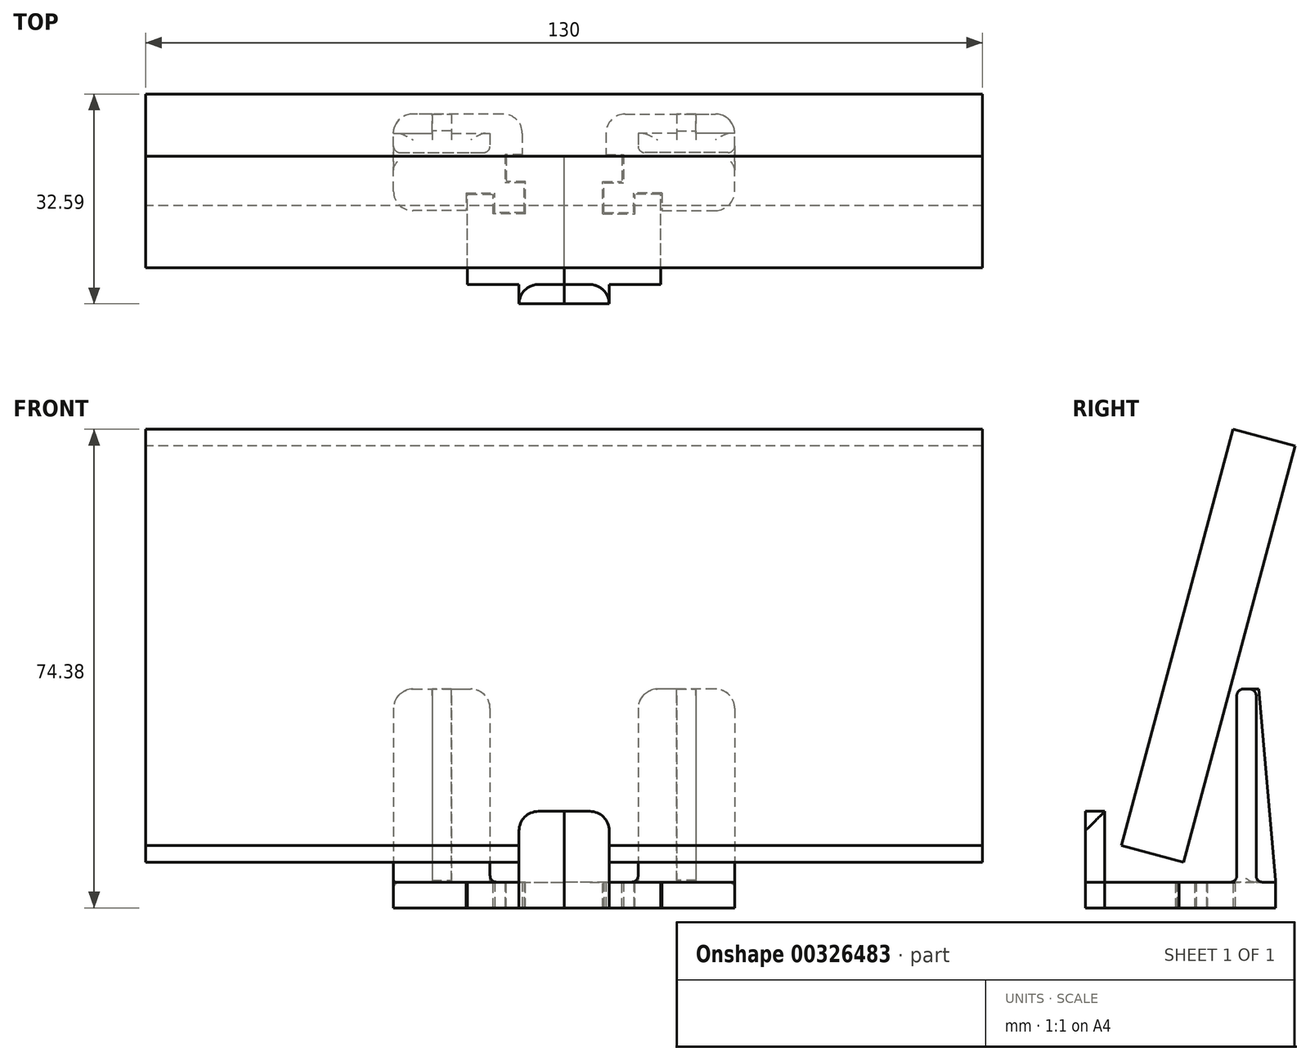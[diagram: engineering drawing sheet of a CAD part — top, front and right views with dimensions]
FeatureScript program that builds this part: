
annotation { "Feature Type Name" : "Feature", "Feature Type Description" : "" }
export const myFeature = defineFeature(function(context is Context, id is Id, definition is map)
    precondition{}
    {
        {
            var Q0;
            Q0=qCreatedBy(makeId("Front.planeOp"),FACE);
            var sketch = newSketch(context, id + "F0", { "sketchPlane" : qUnion([Q0])});
            skLineSegment(sketch, "E0", {"start": v(-35.67, 0) * mm, "end": v(38.03, 0) * mm, "construction": true});
            skSolve(sketch);
        }
        {
            var Q0;
            Q0=sQuery(id+"F0.wireOp",EDGE,"E0");
            cPlane(context, id + "F1", {"entities" : qUnion([Q0]), "cplaneType" : CPlaneType.LINE_ANGLE, "offset" : 25 * mm, "angle" : 345 * degree, "width" : 150 * mm, "height" : 150 * mm});
        }
        {
            var Q0;
            Q0=qCreatedBy(id+"F1.planeOp",FACE);
            var sketch = newSketch(context, id + "F2", { "sketchPlane" : qUnion([Q0])});
            skLineSegment(sketch, "E1.bottom", {"start": v(-65, 77) * mm, "end": v(65, 77) * mm});
            skLineSegment(sketch, "E1.top", {"start": v(-65, 10) * mm, "end": v(65, 10) * mm});
            skLineSegment(sketch, "E1.left", {"start": v(-65, 77) * mm, "end": v(-65, 10) * mm});
            skLineSegment(sketch, "E1.right", {"start": v(65, 77) * mm, "end": v(65, 10) * mm});
            skPoint(sketch, "E2", {"position": v(0, 10) * mm});
            skSolve(sketch);
        }
        {
            var Q0;
            Q0 = qSketchRegion(id + "F2", true);
            extrude(context, id + "F3", {"entities" : qUnion([Q0]), "depth" : 10 * mm});
        }
        {
            var Q0;
            Q0=qCreatedBy(makeId("Right.planeOp"),FACE);
            var sketch = newSketch(context, id + "F4", { "sketchPlane" : qUnion([Q0])});
            skLineSegment(sketch, "E3.bottom", {"start": v(0, 0) * mm, "end": v(20, 0) * mm});
            skLineSegment(sketch, "E3.top", {"start": v(0, 4) * mm, "end": v(20, 4) * mm});
            skLineSegment(sketch, "E3.left", {"start": v(0, 0) * mm, "end": v(0, 4) * mm});
            skLineSegment(sketch, "E3.right", {"start": v(20, 0) * mm, "end": v(20, 4) * mm});
            skLineSegment(sketch, "E4.bottom", {"start": v(0, 0) * mm, "end": v(-3, 0) * mm});
            skLineSegment(sketch, "E4.top", {"start": v(0, 15) * mm, "end": v(-3, 15) * mm});
            skLineSegment(sketch, "E4.left", {"start": v(0, 0) * mm, "end": v(0, 15) * mm});
            skLineSegment(sketch, "E4.right", {"start": v(-3, 0) * mm, "end": v(-3, 15) * mm});
            skSolve(sketch);
        }
        {
            var Q0;
            {var subQ0=sQuery(id+"F4.wireOp",EDGE,"E3.bottom");Q0=makeQuery(id+"F4.imprint","IMPRINT",FACE,{"disambiguationData":[TD([[makeQuery(id+"F4.imprint","IMPRINT",EDGE,{"derivedFrom":subQ0}),1.0]])]});}
            extrude(context, id + "F5", {"entities" : qUnion([Q0]), "oppositeDirection" : true, "depth" : 15 * mm});
        }
        {
            var Q0;
            {var subQ3=sQuery(id+"F4.wireOp",EDGE,"E4.bottom");Q0=makeQuery(id+"F4.imprint","IMPRINT",FACE,{"disambiguationData":[TD([[makeQuery(id+"F4.imprint","IMPRINT",EDGE,{"derivedFrom":subQ3}),-1.0]])]});}
            extrude(context, id + "F6", {"entities" : qUnion([Q0]), "operationType" : NewBodyOperationType.ADD, "oppositeDirection" : true, "depth" : 7 * mm});
        }
        {
            var Q0;
            {var subQ0=makeQuery(id+"F5.opExtrude","SWEPT_FACE",FACE,{"disambiguationData":[OSD([sQuery(id+"F4.wireOp",EDGE,"E3.top")])]});Q0=makeQuery(id+"F9.boolean.opBoolean","MERGE",FACE,{"derivedFrom":[subQ0,makeQuery(id+"F9.opPattern","COPY",FACE,{"derivedFrom":subQ0,"instanceName":"1"})]});}
            var sketch = newSketch(context, id + "F7", { "sketchPlane" : qUnion([Q0])});
            skLineSegment(sketch, "E5.bottom", {"start": v(-15, 20) * mm, "end": v(-9, 20) * mm});
            skLineSegment(sketch, "E5.top", {"start": v(-15, 14) * mm, "end": v(-9, 14) * mm});
            skLineSegment(sketch, "E5.left", {"start": v(-15, 20) * mm, "end": v(-15, 14) * mm});
            skLineSegment(sketch, "E5.right", {"start": v(-9, 20) * mm, "end": v(-9, 14) * mm});
            skLineSegment(sketch, "E6.bottom", {"start": v(-6, 11) * mm, "end": v(-11, 11) * mm});
            skLineSegment(sketch, "E6.top", {"start": v(-6, 16) * mm, "end": v(-11, 16) * mm});
            skLineSegment(sketch, "E6.left", {"start": v(-6, 11) * mm, "end": v(-6, 16) * mm});
            skLineSegment(sketch, "E6.right", {"start": v(-11, 11) * mm, "end": v(-11, 16) * mm});
            skSolve(sketch);
        }
        {
            var Q0;
            Q0 = qSketchRegion(id + "F7", true);
            extrude(context, id + "F8", {"entities" : qUnion([Q0]), "operationType" : NewBodyOperationType.REMOVE, "endBound" : BoundingType.UP_TO_NEXT, "oppositeDirection" : true, "depth" : 25 * mm});
        }
        {
            var Q0;
            Q0=makeQuery(id+"F5.opExtrude","SWEPT_BODY",BODY,{"disambiguationData":[OSD([sQuery(id+"F4.wireOp",EDGE,"E3.bottom"),sQuery(id+"F4.wireOp",EDGE,"E3.top"),sQuery(id+"F4.wireOp",EDGE,"E3.right"),sQuery(id+"F4.wireOp",EDGE,"E4.left")])]});
            var Q1;
            {var subQ0=sQuery(id+"F4.wireOp",EDGE,"E3.bottom");Q1=makeQuery(id+"F4.imprint","IMPRINT",FACE,{"disambiguationData":[TD([[makeQuery(id+"F4.imprint","IMPRINT",EDGE,{"derivedFrom":subQ0}),1.0]])]});}
            mirror(context, id + "F9", {"operationType" : NewBodyOperationType.ADD, "entities" : qUnion([Q0]), "mirrorPlane" : qUnion([Q1])});
        }
        {
            var Q0;
            Q0=qCreatedBy(makeId("Top.planeOp"),FACE);
            var sketch = newSketch(context, id + "F10", { "sketchPlane" : qUnion([Q0])});
            skLineSegment(sketch, "E7.top", {"start": v(-6.5, 26.5) * mm, "end": v(-26.5, 26.5) * mm});
            skLineSegment(sketch, "E7.right", {"start": v(-26.5, 11.5) * mm, "end": v(-26.5, 26.5) * mm});
            skLineSegment(sketch, "E8", {"start": v(-15.2, 11.5) * mm, "end": v(-26.5, 11.5) * mm});
            skLineSegment(sketch, "E9", {"start": v(-6.5, 26.5) * mm, "end": v(-6.5, 20.2) * mm});
            skLineSegment(sketch, "E10", {"start": v(-15, 14) * mm, "end": v(-15, 12.25) * mm, "construction": true});
            skLineSegment(sketch, "E11", {"start": v(-6.5, 20) * mm, "end": v(-9, 20) * mm, "construction": true});
            skLineSegment(sketch, "E12.0", {"start": v(-9, 20) * mm, "end": v(-9, 16) * mm, "construction": true});
            skLineSegment(sketch, "E13.0", {"start": v(-6, 16) * mm, "end": v(-9, 16) * mm, "construction": true});
            skLineSegment(sketch, "E14.0", {"start": v(-6, 11) * mm, "end": v(-6, 16) * mm, "construction": true});
            skLineSegment(sketch, "E15.0", {"start": v(-6, 11) * mm, "end": v(-11, 11) * mm, "construction": true});
            skLineSegment(sketch, "E16.0", {"start": v(-11, 11) * mm, "end": v(-11, 14) * mm, "construction": true});
            skLineSegment(sketch, "E17.0", {"start": v(-15, 14) * mm, "end": v(-11, 14) * mm, "construction": true});
            skLineSegment(sketch, "E18.0", {"start": v(-15.2, 14.2) * mm, "end": v(-15.2, 11.5) * mm});
            skLineSegment(sketch, "E18.1", {"start": v(-15.2, 14.2) * mm, "end": v(-10.8, 14.2) * mm});
            skLineSegment(sketch, "E18.2", {"start": v(-10.8, 11.2) * mm, "end": v(-10.8, 14.2) * mm});
            skLineSegment(sketch, "E18.3", {"start": v(-6.2, 11.2) * mm, "end": v(-10.8, 11.2) * mm});
            skLineSegment(sketch, "E18.4", {"start": v(-6.5, 20.2) * mm, "end": v(-9.2, 20.2) * mm});
            skLineSegment(sketch, "E18.5", {"start": v(-9.2, 20.2) * mm, "end": v(-9.2, 15.8) * mm});
            skLineSegment(sketch, "E18.6", {"start": v(-6.2, 15.8) * mm, "end": v(-9.2, 15.8) * mm});
            skLineSegment(sketch, "E18.7", {"start": v(-6.2, 11.2) * mm, "end": v(-6.2, 15.8) * mm});
            skSolve(sketch);
        }
        {
            var Q0;
            Q0 = qSketchRegion(id + "F10", true);
            extrude(context, id + "F11", {"entities" : qUnion([Q0]), "depth" : 4 * mm});
        }
        {
            var Q0;
            Q0=makeQuery(id+"F11.opExtrude","CAP_FACE",FACE,{"disambiguationData":[OSD([sQuery(id+"F10.wireOp",EDGE,"E7.top"),sQuery(id+"F10.wireOp",EDGE,"E7.right"),sQuery(id+"F10.wireOp",EDGE,"E8"),sQuery(id+"F10.wireOp",EDGE,"E9"),sQuery(id+"F10.wireOp",EDGE,"E18.0"),sQuery(id+"F10.wireOp",EDGE,"E18.1"),sQuery(id+"F10.wireOp",EDGE,"E18.2"),sQuery(id+"F10.wireOp",EDGE,"E18.3"),sQuery(id+"F10.wireOp",EDGE,"E18.4"),sQuery(id+"F10.wireOp",EDGE,"E18.5"),sQuery(id+"F10.wireOp",EDGE,"E18.6"),sQuery(id+"F10.wireOp",EDGE,"E18.7")])],"isStart":false});
            var sketch = newSketch(context, id + "F12", { "sketchPlane" : qUnion([Q0])});
            skLineSegment(sketch, "E19.bottom", {"start": v(-26.5, 23.5) * mm, "end": v(-11.5, 23.5) * mm});
            skLineSegment(sketch, "E19.top", {"start": v(-26.5, 20.5) * mm, "end": v(-11.5, 20.5) * mm});
            skLineSegment(sketch, "E19.left", {"start": v(-26.5, 23.5) * mm, "end": v(-26.5, 20.5) * mm});
            skLineSegment(sketch, "E19.right", {"start": v(-11.5, 23.5) * mm, "end": v(-11.5, 20.5) * mm});
            skPoint(sketch, "E20", {"position": v(-19, 23.5) * mm});
            skLineSegment(sketch, "E21.bottom", {"start": v(-17.5, 26.5) * mm, "end": v(-20.5, 26.5) * mm});
            skLineSegment(sketch, "E21.top", {"start": v(-17.5, 23.5) * mm, "end": v(-20.5, 23.5) * mm});
            skLineSegment(sketch, "E21.left", {"start": v(-17.5, 26.5) * mm, "end": v(-17.5, 23.5) * mm});
            skLineSegment(sketch, "E21.right", {"start": v(-20.5, 26.5) * mm, "end": v(-20.5, 23.5) * mm});
            skSolve(sketch);
        }
        {
            var Q0;
            Q0 = qSketchRegion(id + "F12", true);
            extrude(context, id + "F13", {"entities" : qUnion([Q0]), "operationType" : NewBodyOperationType.ADD, "depth" : 30 * mm});
        }
        {
            var Q0;
            Q0=makeQuery(id+"F13.opExtrude","CAP_EDGE",EDGE,{"disambiguationData":[OSD([sQuery(id+"F12.wireOp",EDGE,"E21.bottom")])],"isStart":false});
            chamfer(context, id + "F14", {"entities" : qUnion([Q0]), "chamferType" : ChamferType.OFFSET_ANGLE, "width" : 2.6 * mm, "oppositeDirection" : false, "angle" : 85 * degree, "tangentPropagation" : true});
        }
        {
            var Q0;
            Q0=makeQuery(id+"F11.opExtrude","SWEPT_EDGE",EDGE,{"disambiguationData":[OSD([sQuery(id+"F10.wireOp",EDGE,"E7.right"),sQuery(id+"F10.wireOp",EDGE,"E8")])]});
            var Q1;
            Q1=makeQuery(id+"F11.opExtrude","SWEPT_EDGE",EDGE,{"disambiguationData":[OSD([sQuery(id+"F10.wireOp",EDGE,"E7.top"),sQuery(id+"F10.wireOp",EDGE,"E7.right")])]});
            var Q2;
            Q2=makeQuery(id+"F5.opExtrude","CAP_EDGE",EDGE,{"disambiguationData":[OSD([sQuery(id+"F4.wireOp",EDGE,"E4.left")])],"isStart":false});
            var Q3;
            {var subQ0=sQuery(id+"F4.wireOp",EDGE,"E4.left");Q3=makeQuery(id+"F6.boolean.opBoolean","SPLIT",EDGE,{"disambiguationData":[topologyDisambiguationEdgeConnected([makeQuery(id+"F5.opExtrude","SWEPT_FACE",FACE,{"disambiguationData":[OSD([subQ0])]})])],"derivedFrom":makeQuery(id+"F6.opExtrude","CAP_EDGE",EDGE,{"disambiguationData":[OSD([subQ0])],"isStart":false})});}
            var Q4;
            {var subQ0=sQuery(id+"F4.wireOp",EDGE,"E4.left");Q4=makeQuery(id+"F9.opPattern","COPY",EDGE,{"derivedFrom":makeQuery(id+"F6.boolean.opBoolean","SPLIT",EDGE,{"disambiguationData":[topologyDisambiguationEdgeConnected([makeQuery(id+"F5.opExtrude","SWEPT_FACE",FACE,{"disambiguationData":[OSD([subQ0])]})])],"derivedFrom":makeQuery(id+"F6.opExtrude","CAP_EDGE",EDGE,{"disambiguationData":[OSD([subQ0])],"isStart":false})}),"instanceName":"1"});}
            var Q5;
            Q5=makeQuery(id+"F9.opPattern","COPY",EDGE,{"derivedFrom":makeQuery(id+"F5.opExtrude","CAP_EDGE",EDGE,{"disambiguationData":[OSD([sQuery(id+"F4.wireOp",EDGE,"E4.left")])],"isStart":false}),"instanceName":"1"});
            var Q6;
            Q6=makeQuery(id+"F11.opExtrude","SWEPT_EDGE",EDGE,{"disambiguationData":[OSD([sQuery(id+"F10.wireOp",EDGE,"E7.top"),sQuery(id+"F10.wireOp",EDGE,"E9")])]});
            var Q7;
            Q7=makeQuery(id+"F6.opExtrude","CAP_EDGE",EDGE,{"disambiguationData":[OSD([sQuery(id+"F4.wireOp",EDGE,"E4.top")])],"isStart":false});
            var Q8;
            Q8=makeQuery(id+"F9.opPattern","COPY",EDGE,{"derivedFrom":makeQuery(id+"F6.opExtrude","CAP_EDGE",EDGE,{"disambiguationData":[OSD([sQuery(id+"F4.wireOp",EDGE,"E4.top")])],"isStart":false}),"instanceName":"1"});
            var Q9;
            Q9=makeQuery(id+"F13.opExtrude","CAP_EDGE",EDGE,{"disambiguationData":[OSD([sQuery(id+"F12.wireOp",EDGE,"E19.left")])],"isStart":false});
            var Q10;
            Q10=makeQuery(id+"F13.opExtrude","CAP_EDGE",EDGE,{"disambiguationData":[OSD([sQuery(id+"F12.wireOp",EDGE,"E19.right")])],"isStart":false});
            fillet(context, id + "F15", {"entities" : qUnion([Q0, Q1, Q2, Q3, Q4, Q5, Q6, Q7, Q8, Q9, Q10]), "radius" : 3 * mm, "tangentPropagation" : true, "allowEdgeOverflow" : false});
        }
        {
            var Q0;
            Q0=makeQuery(id+"F13.opExtrude","SWEPT_FACE",FACE,{"disambiguationData":[OSD([sQuery(id+"F12.wireOp",EDGE,"E19.top")])]});
            var Q1;
            {var subQ0=makeQuery(id+"F6.opExtrude","SWEPT_FACE",FACE,{"disambiguationData":[OSD([sQuery(id+"F4.wireOp",EDGE,"E4.left")])]});Q1=makeQuery(id+"F9.boolean.opBoolean","MERGE",FACE,{"derivedFrom":[subQ0,makeQuery(id+"F9.opPattern","COPY",FACE,{"derivedFrom":subQ0,"instanceName":"1"})]});}
            var Q2;
            {var subQ0=makeQuery(id+"F6.opExtrude","SWEPT_EDGE",EDGE,{"disambiguationData":[OSD([sQuery(id+"F4.wireOp",EDGE,"E4.top"),sQuery(id+"F4.wireOp",EDGE,"E4.right")])]});Q2=makeQuery(id+"F9.boolean.opBoolean","MERGE",EDGE,{"derivedFrom":[subQ0,makeQuery(id+"F9.opPattern","COPY",EDGE,{"derivedFrom":subQ0,"instanceName":"1"})]});}
            var Q3;
            {var subQ0=sQuery(id+"F12.wireOp",EDGE,"E19.bottom");Q3=makeQuery(id+"F13.opExtrude","CAP_EDGE",EDGE,{"disambiguationData":[OSD([subQ0]),TDD([makeQuery(id+"F12.imprint","IMPRINT",EDGE,{"disambiguationData":[TD([[makeQuery(id+"F12.imprint","INTERSECT",VERTEX,{"derivedFrom":[subQ0,sQuery(id+"F12.wireOp",EDGE,"E19.right")]}),1.0]])],"derivedFrom":subQ0})])],"isStart":false});}
            var Q4;
            {var subQ0=sQuery(id+"F12.wireOp",EDGE,"E19.bottom");Q4=makeQuery(id+"F13.opExtrude","CAP_EDGE",EDGE,{"disambiguationData":[OSD([subQ0]),TDD([makeQuery(id+"F12.imprint","IMPRINT",EDGE,{"disambiguationData":[TD([[makeQuery(id+"F12.imprint","INTERSECT",VERTEX,{"derivedFrom":[makeQuery(id+"F11.opExtrude","CAP_EDGE",EDGE,{"disambiguationData":[OSD([sQuery(id+"F10.wireOp",EDGE,"E7.right")])],"isStart":false}),subQ0,sQuery(id+"F12.wireOp",EDGE,"E19.left")]}),-1.0]])],"derivedFrom":subQ0})])],"isStart":false});}
            var Q5;
            {var subQ0=sQuery(id+"F12.wireOp",EDGE,"E19.bottom");Q5=makeQuery(id+"F13.opExtrude","CAP_EDGE",EDGE,{"disambiguationData":[OSD([subQ0]),TDD([makeQuery(id+"F12.imprint","IMPRINT",EDGE,{"disambiguationData":[TD([[makeQuery(id+"F12.imprint","INTERSECT",VERTEX,{"derivedFrom":[makeQuery(id+"F11.opExtrude","CAP_EDGE",EDGE,{"disambiguationData":[OSD([sQuery(id+"F10.wireOp",EDGE,"E7.right")])],"isStart":false}),subQ0,sQuery(id+"F12.wireOp",EDGE,"E19.left")]}),-1.0]])],"derivedFrom":subQ0})])],"isStart":true});}
            var Q6;
            {var subQ0=sQuery(id+"F12.wireOp",EDGE,"E19.bottom");Q6=makeQuery(id+"F13.opExtrude","CAP_EDGE",EDGE,{"disambiguationData":[OSD([subQ0]),TDD([makeQuery(id+"F12.imprint","IMPRINT",EDGE,{"disambiguationData":[TD([[makeQuery(id+"F12.imprint","INTERSECT",VERTEX,{"derivedFrom":[subQ0,sQuery(id+"F12.wireOp",EDGE,"E19.right")]}),1.0]])],"derivedFrom":subQ0})])],"isStart":true});}
            var Q7;
            Q7=makeQuery(id+"F13.opExtrude","CAP_EDGE",EDGE,{"disambiguationData":[OSD([sQuery(id+"F12.wireOp",EDGE,"E19.right")])],"isStart":true});
            fillet(context, id + "F16", {"entities" : qUnion([Q0, Q1, Q2, Q3, Q4, Q5, Q6, Q7]), "radius" : 1 * mm, "allowEdgeOverflow" : false});
        }
        {
            var Q0;
            Q0=makeQuery(id+"F11.opExtrude","SWEPT_BODY",BODY,{"disambiguationData":[OSD([sQuery(id+"F10.wireOp",EDGE,"E7.top"),sQuery(id+"F10.wireOp",EDGE,"E7.right"),sQuery(id+"F10.wireOp",EDGE,"E8"),sQuery(id+"F10.wireOp",EDGE,"E9"),sQuery(id+"F10.wireOp",EDGE,"E18.0"),sQuery(id+"F10.wireOp",EDGE,"E18.1"),sQuery(id+"F10.wireOp",EDGE,"E18.2"),sQuery(id+"F10.wireOp",EDGE,"E18.3"),sQuery(id+"F10.wireOp",EDGE,"E18.4"),sQuery(id+"F10.wireOp",EDGE,"E18.5"),sQuery(id+"F10.wireOp",EDGE,"E18.6"),sQuery(id+"F10.wireOp",EDGE,"E18.7")])]});
            var Q1;
            Q1=qCreatedBy(makeId("Right.planeOp"),FACE);
            mirror(context, id + "F17", {"entities" : qUnion([Q0]), "mirrorPlane" : qUnion([Q1])});
        }
    });
